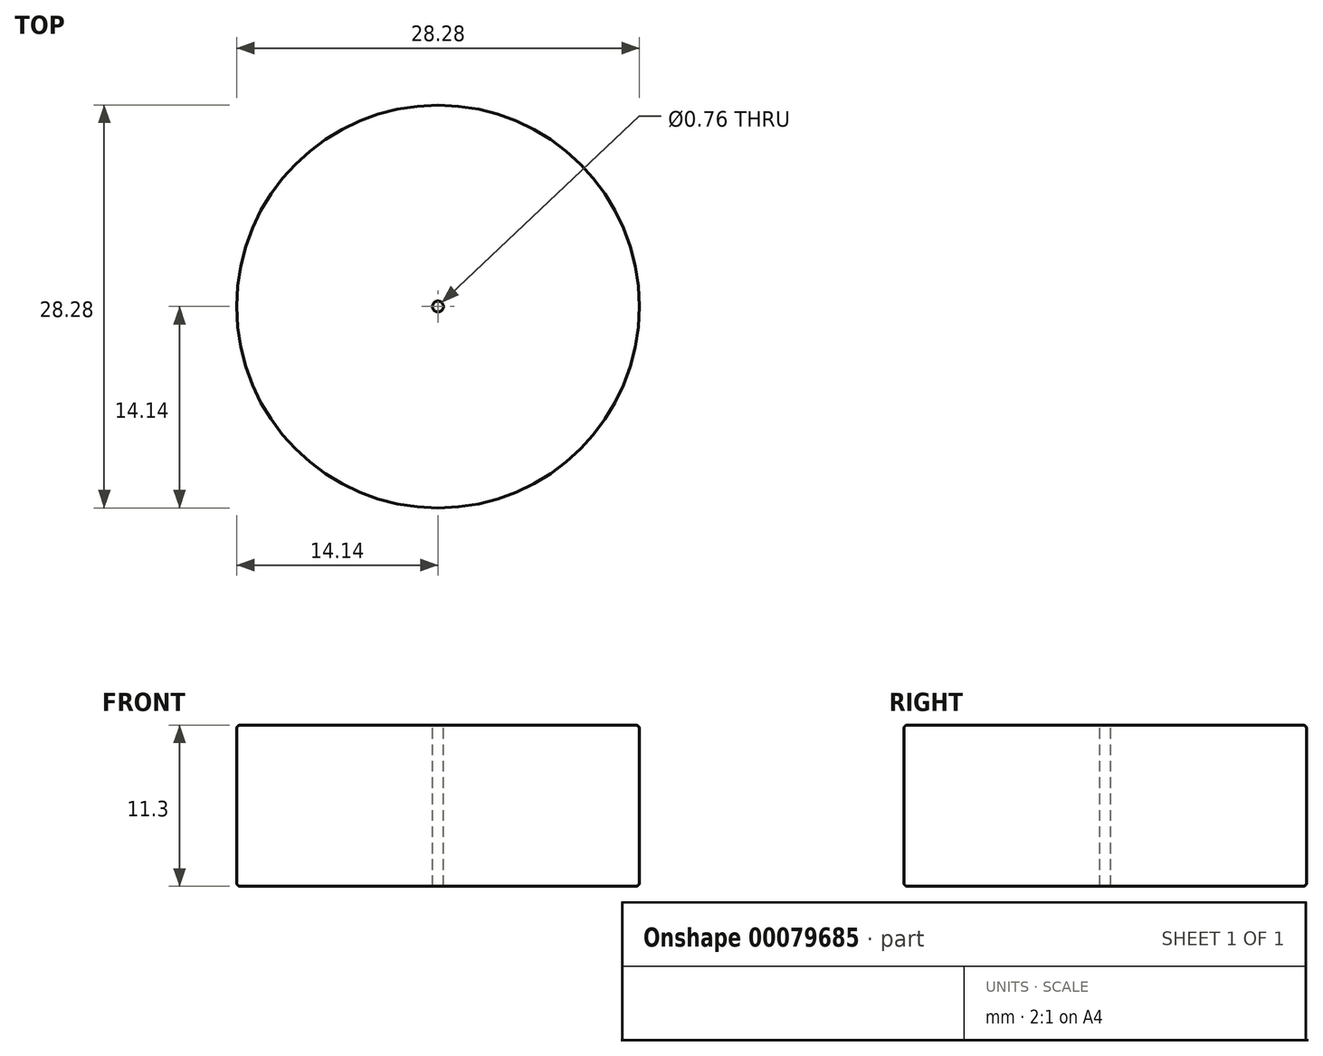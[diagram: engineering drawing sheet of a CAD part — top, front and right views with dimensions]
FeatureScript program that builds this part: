
annotation { "Feature Type Name" : "Feature", "Feature Type Description" : "" }
export const myFeature = defineFeature(function(context is Context, id is Id, definition is map)
    precondition{}
    {
        {
            var Q0;
            Q0=qCreatedBy(makeId("Top.planeOp"),FACE);
            var sketch = newSketch(context, id + "F0", { "sketchPlane" : qUnion([Q0])});
            skCircle(sketch, "E0", {"center": v(0, 0) * mm, "radius": 14.14 * mm});
            skSolve(sketch);
        }
        {
            var Q0;
            Q0 = qSketchRegion(id + "F0", true);
            extrude(context, id + "F1", {"entities" : qUnion([Q0]), "depth" : 11.3 * mm});
        }
        {
            var Q0;
            Q0=makeQuery(id+"F1.opExtrude","CAP_EDGE",EDGE,{"disambiguationData":[OSD([sQuery(id+"F0.wireOp",EDGE,"E0")])],"isStart":false});
            var Q1;
            Q1=makeQuery(id+"F1.opExtrude","CAP_EDGE",EDGE,{"disambiguationData":[OSD([sQuery(id+"F0.wireOp",EDGE,"E0")])],"isStart":true});
            fillet(context, id + "F2", {"entities" : qUnion([Q0, Q1]), "radius" : 0.25 * mm, "tangentPropagation" : true, "allowEdgeOverflow" : false});
        }
        {
            var Q0;
            Q0=makeQuery(id+"F1.opExtrude","CAP_FACE",FACE,{"disambiguationData":[OSD([sQuery(id+"F0.wireOp",EDGE,"E0")])],"isStart":false});
            var sketch = newSketch(context, id + "F3", { "sketchPlane" : qUnion([Q0])});
            skCircle(sketch, "E1", {"center": v(0, 0) * mm, "radius": 0.38 * mm});
            skSolve(sketch);
        }
        {
            var Q0;
            Q0 = qSketchRegion(id + "F3", true);
            extrude(context, id + "F4", {"entities" : qUnion([Q0]), "operationType" : NewBodyOperationType.REMOVE, "oppositeDirection" : true, "depth" : 25.4 * mm});
        }
    });
